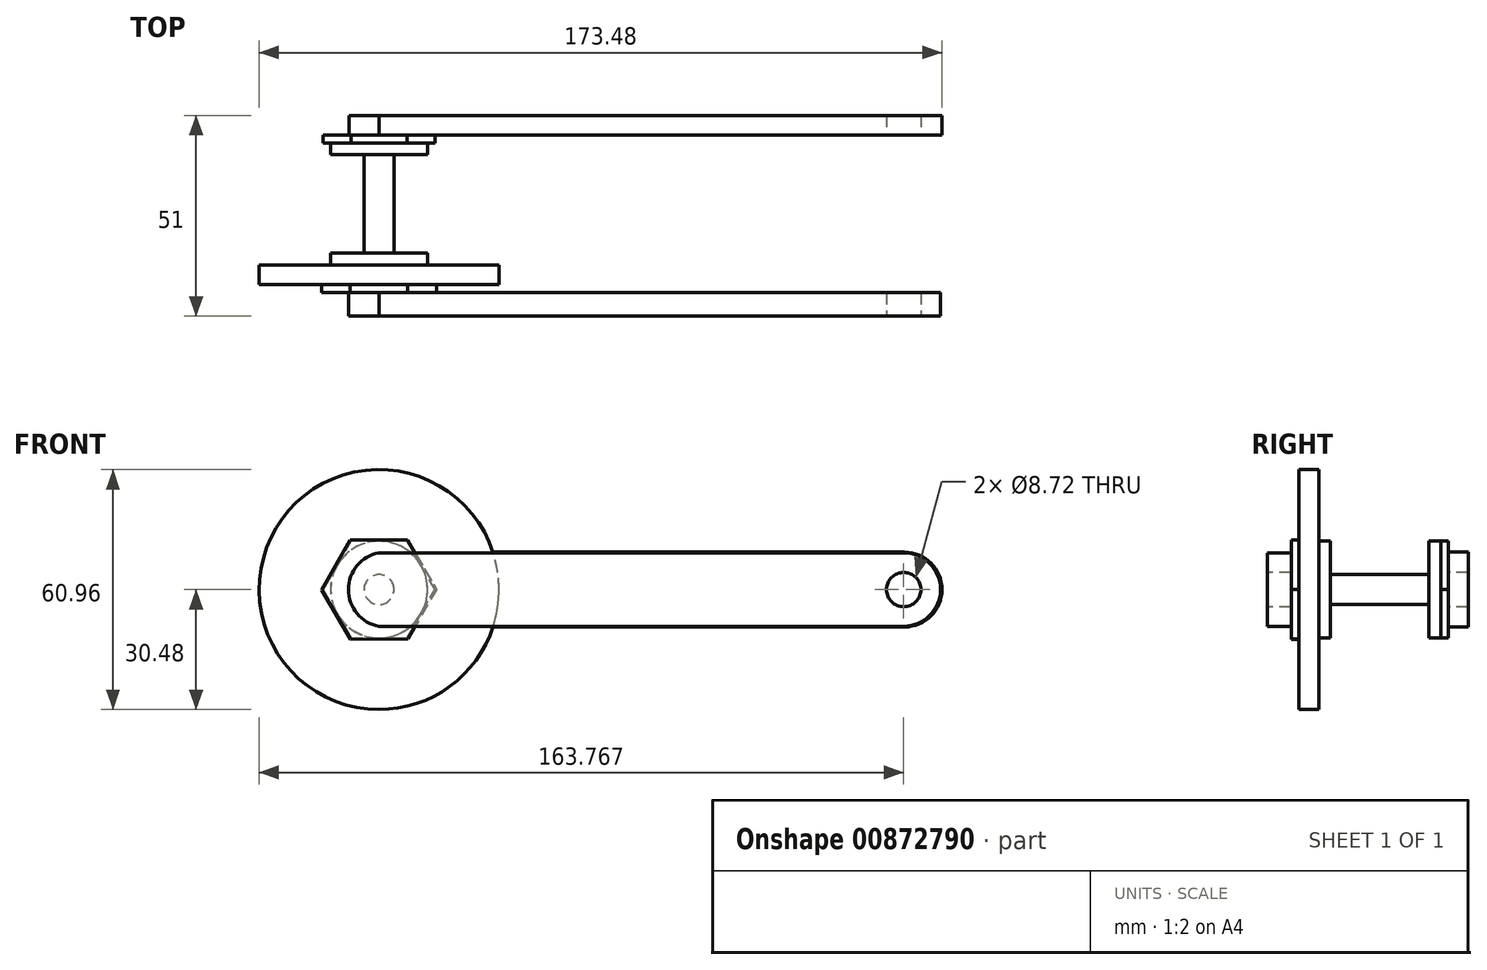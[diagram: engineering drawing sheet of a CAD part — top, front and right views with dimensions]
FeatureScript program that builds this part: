
annotation { "Feature Type Name" : "Feature", "Feature Type Description" : "" }
export const myFeature = defineFeature(function(context is Context, id is Id, definition is map)
    precondition{}
    {
        {
            var Q0;
            Q0=qCreatedBy(makeId("Front.planeOp"),FACE);
            var sketch = newSketch(context, id + "F0", { "sketchPlane" : qUnion([Q0])});
            skCircle(sketch, "E0", {"center": v(0, 0) * mm, "radius": 30.48 * mm});
            skCircle(sketch, "E1", {"center": v(-75.03, 0) * mm, "radius": 15.2 * mm});
            skSolve(sketch);
        }
        {
            var Q0;
            Q0=makeQuery(id+"F0.imprint","IMPRINT",FACE,{"disambiguationData":[TD([[makeQuery(id+"F0.imprint","IMPRINT",EDGE,{"derivedFrom":sQuery(id+"F0.wireOp",EDGE,"E0")}),1.0]])]});
            extrude(context, id + "F1", {"entities" : qUnion([Q0]), "depth" : 5 * mm, "offsetDistance" : 25 * mm});
        }
        {
            var Q0;
            Q0=makeQuery(id+"F1.opExtrude","CAP_FACE",FACE,{"disambiguationData":[OSD([sQuery(id+"F0.wireOp",EDGE,"E0")])],"isStart":true});
            var sketch = newSketch(context, id + "F2", { "sketchPlane" : qUnion([Q0])});
            skCircle(sketch, "E2", {"center": v(0, 0) * mm, "radius": 12.32 * mm});
            skSolve(sketch);
        }
        {
            var Q0;
            Q0=makeQuery(id+"F2.imprint","IMPRINT",FACE,{"disambiguationData":[TD([[makeQuery(id+"F2.imprint","IMPRINT",EDGE,{"derivedFrom":sQuery(id+"F2.wireOp",EDGE,"E2")}),1.0]])]});
            extrude(context, id + "F3", {"entities" : qUnion([Q0]), "operationType" : NewBodyOperationType.ADD, "depth" : 3 * mm, "offsetDistance" : 25 * mm});
        }
        {
            var Q0;
            Q0=makeQuery(id+"F3.opExtrude","CAP_FACE",FACE,{"disambiguationData":[OSD([sQuery(id+"F2.wireOp",EDGE,"E2")])],"isStart":false});
            var sketch = newSketch(context, id + "F4", { "sketchPlane" : qUnion([Q0])});
            skCircle(sketch, "E3", {"center": v(0, 0) * mm, "radius": 3.82 * mm});
            skSolve(sketch);
        }
        {
            var Q0;
            Q0=makeQuery(id+"F4.imprint","IMPRINT",FACE,{"disambiguationData":[TD([[makeQuery(id+"F4.imprint","IMPRINT",EDGE,{"derivedFrom":sQuery(id+"F4.wireOp",EDGE,"E3")}),1.0]])]});
            extrude(context, id + "F5", {"entities" : qUnion([Q0]), "operationType" : NewBodyOperationType.ADD, "depth" : 25 * mm, "offsetDistance" : 25 * mm});
        }
        {
            var Q0;
            Q0=makeQuery(id+"F5.opExtrude","CAP_FACE",FACE,{"disambiguationData":[OSD([sQuery(id+"F4.wireOp",EDGE,"E3")])],"isStart":false});
            var sketch = newSketch(context, id + "F6", { "sketchPlane" : qUnion([Q0])});
            skCircle(sketch, "E4", {"center": v(0, 0) * mm, "radius": 12.3 * mm});
            skSolve(sketch);
        }
        {
            var Q0;
            Q0 = qSketchRegion(id + "F6", true);
            extrude(context, id + "F7", {"entities" : qUnion([Q0]), "operationType" : NewBodyOperationType.ADD, "depth" : 3 * mm, "offsetDistance" : 25 * mm});
        }
        {
            var Q0;
            Q0=makeQuery(id+"F1.opExtrude","CAP_FACE",FACE,{"disambiguationData":[OSD([sQuery(id+"F0.wireOp",EDGE,"E0")])],"isStart":false});
            var sketch = newSketch(context, id + "F8", { "sketchPlane" : qUnion([Q0])});
            skCircle(sketch, "E5.cCircle", {"center": v(0, 0) * mm, "radius": 12.63 * mm, "construction": true});
            skLineSegment(sketch, "E5.0", {"start": v(-14.58, -0.07) * mm, "end": v(-7.35, 12.6) * mm});
            skLineSegment(sketch, "E5.1", {"start": v(-7.35, 12.6) * mm, "end": v(7.23, 12.66) * mm});
            skLineSegment(sketch, "E5.2", {"start": v(7.23, 12.66) * mm, "end": v(14.58, 0.07) * mm});
            skLineSegment(sketch, "E5.3", {"start": v(14.58, 0.07) * mm, "end": v(7.35, -12.6) * mm});
            skLineSegment(sketch, "E5.4", {"start": v(7.35, -12.6) * mm, "end": v(-7.23, -12.66) * mm});
            skLineSegment(sketch, "E5.5", {"start": v(-7.23, -12.66) * mm, "end": v(-14.58, -0.07) * mm});
            skPoint(sketch, "E5.0.midPoint", {"position": v(-10.97, 6.26) * mm});
            skSolve(sketch);
        }
        {
            var Q0;
            Q0 = qSketchRegion(id + "F8", true);
            extrude(context, id + "F9", {"entities" : qUnion([Q0]), "operationType" : NewBodyOperationType.ADD, "depth" : 2 * mm, "offsetDistance" : 25 * mm});
        }
        {
            var Q0;
            Q0=makeQuery(id+"F9.opExtrude","CAP_FACE",FACE,{"disambiguationData":[OSD([sQuery(id+"F8.wireOp",EDGE,"E5.0"),sQuery(id+"F8.wireOp",EDGE,"E5.1"),sQuery(id+"F8.wireOp",EDGE,"E5.2"),sQuery(id+"F8.wireOp",EDGE,"E5.3"),sQuery(id+"F8.wireOp",EDGE,"E5.4"),sQuery(id+"F8.wireOp",EDGE,"E5.5")])],"isStart":false});
            var sketch = newSketch(context, id + "F10", { "sketchPlane" : qUnion([Q0])});
            skLineSegment(sketch, "E6.bottom", {"start": v(0, 9.34) * mm, "end": v(133.29, 9.34) * mm});
            skLineSegment(sketch, "E6.top", {"start": v(0, -9.34) * mm, "end": v(133.29, -9.34) * mm});
            skLineSegment(sketch, "E6.left", {"start": v(0, 9.34) * mm, "end": v(0, -9.34) * mm});
            skLineSegment(sketch, "E6.right", {"start": v(133.29, 9.34) * mm, "end": v(133.29, -9.34) * mm});
            skArc(sketch, "E7", {"start": v(0, 9.34) * mm, "mid": v(-7.78, 0) * mm, "end": v(0, -9.34) * mm});
            skArc(sketch, "E8", {"start": v(133.29, -9.34) * mm, "mid": v(142.63, 0) * mm, "end": v(133.29, 9.34) * mm});
            skSolve(sketch);
        }
        {
            var Q0;
            Q0 = qSketchRegion(id + "F10", true);
            extrude(context, id + "F11", {"entities" : qUnion([Q0]), "operationType" : NewBodyOperationType.ADD, "depth" : 6 * mm, "offsetDistance" : 25 * mm});
        }
        {
            var Q0;
            Q0=makeQuery(id+"F7.opExtrude","CAP_FACE",FACE,{"disambiguationData":[OSD([sQuery(id+"F6.wireOp",EDGE,"E4")])],"isStart":false});
            var sketch = newSketch(context, id + "F12", { "sketchPlane" : qUnion([Q0])});
            skCircle(sketch, "E9.cCircle", {"center": v(0, 0) * mm, "radius": 12.3 * mm, "construction": true});
            skLineSegment(sketch, "E9.0", {"start": v(-7.1, 12.3) * mm, "end": v(7.1, 12.3) * mm});
            skLineSegment(sketch, "E9.1", {"start": v(7.1, 12.3) * mm, "end": v(14.2, 0) * mm});
            skLineSegment(sketch, "E9.2", {"start": v(14.2, 0) * mm, "end": v(7.1, -12.3) * mm});
            skLineSegment(sketch, "E9.3", {"start": v(7.1, -12.3) * mm, "end": v(-7.1, -12.3) * mm});
            skLineSegment(sketch, "E9.4", {"start": v(-7.1, -12.3) * mm, "end": v(-14.2, 0) * mm});
            skLineSegment(sketch, "E9.5", {"start": v(-14.2, 0) * mm, "end": v(-7.1, 12.3) * mm});
            skPoint(sketch, "E9.0.midPoint", {"position": v(0, 12.3) * mm});
            skSolve(sketch);
        }
        {
            var Q0;
            Q0 = qSketchRegion(id + "F12", true);
            extrude(context, id + "F13", {"entities" : qUnion([Q0]), "operationType" : NewBodyOperationType.ADD, "depth" : 2 * mm, "offsetDistance" : 25 * mm});
        }
        {
            var Q0;
            Q0=makeQuery(id+"F13.opExtrude","CAP_FACE",FACE,{"disambiguationData":[OSD([sQuery(id+"F12.wireOp",EDGE,"E9.0"),sQuery(id+"F12.wireOp",EDGE,"E9.1"),sQuery(id+"F12.wireOp",EDGE,"E9.2"),sQuery(id+"F12.wireOp",EDGE,"E9.3"),sQuery(id+"F12.wireOp",EDGE,"E9.4"),sQuery(id+"F12.wireOp",EDGE,"E9.5")])],"isStart":false});
            var sketch = newSketch(context, id + "F14", { "sketchPlane" : qUnion([Q0])});
            skLineSegment(sketch, "E10.bottom", {"start": v(0, -9.5) * mm, "end": v(-133.5, -9.5) * mm});
            skLineSegment(sketch, "E10.top", {"start": v(0, 9.5) * mm, "end": v(-133.5, 9.5) * mm});
            skLineSegment(sketch, "E10.left", {"start": v(0, -9.5) * mm, "end": v(0, 9.5) * mm});
            skLineSegment(sketch, "E10.right", {"start": v(-133.5, -9.5) * mm, "end": v(-133.5, 9.5) * mm});
            skArc(sketch, "E11", {"start": v(-133.5, 9.5) * mm, "mid": v(-143, 0) * mm, "end": v(-133.5, -9.5) * mm});
            skArc(sketch, "E12", {"start": v(0, -9.5) * mm, "mid": v(7.61, 0) * mm, "end": v(0, 9.5) * mm});
            skSolve(sketch);
        }
        {
            var Q0;
            Q0 = qSketchRegion(id + "F14", true);
            extrude(context, id + "F15", {"entities" : qUnion([Q0]), "operationType" : NewBodyOperationType.ADD, "depth" : 5 * mm, "offsetDistance" : 25 * mm});
        }
        {
            var Q0;
            Q0=makeQuery(id+"F11.opExtrude","CAP_FACE",FACE,{"disambiguationData":[OSD([sQuery(id+"F10.wireOp",EDGE,"E6.bottom"),sQuery(id+"F10.wireOp",EDGE,"E6.top"),sQuery(id+"F10.wireOp",EDGE,"E7"),sQuery(id+"F10.wireOp",EDGE,"E8")])],"isStart":false});
            var sketch = newSketch(context, id + "F16", { "sketchPlane" : qUnion([Q0])});
            skCircle(sketch, "E13", {"center": v(133.29, 0) * mm, "radius": 4.36 * mm});
            skSolve(sketch);
        }
        {
            var Q0;
            Q0 = qSketchRegion(id + "F16", true);
            extrude(context, id + "F17", {"entities" : qUnion([Q0]), "operationType" : NewBodyOperationType.REMOVE, "oppositeDirection" : true, "depth" : 55 * mm, "offsetDistance" : 25 * mm});
        }
    });
